# Revit family: Dachhalter BIG FOOT 400
name_source: partatom
category: HLS-Bauteile
units: mm (PartAtom-declared; Revit-internal decimal feet)

## family parameters
Arbeitsebenenbasiert = Ja
Beim Laden mit Abzugskörper schneiden = Nein
Bemaßung runder Anschluss = Durchmesser verwenden
Beschriftungsausrichtung beibehalten = Nein
Gemeinsam genutzt = Ja
Immer vertikal = Nein
Klassifizierung = Keine
Raumberechnungspunkt = Nein
Teiletyp = Normal

## types (1)
- Dachhalter BIG FOOT 400
    Artikelnummer = 08197625
    Breite Platte = 400 mm  [stored 1.31234 ft]
    EAN = 4250928468925
    Fabrikat = MEFA
    Gewicht = 1,90 kg
    Gewicht pro Bauteil = 1,90 kg
    Kurztext1 = Dachhalter BIG FOOT® 400
    Kurztext2 = für C-Profil 45/45
    Länge Platte = 400 mm  [stored 1.31234 ft]
    Material = Kunststoff
    Materialname = Polyamid 6
    Mengeneinheit = St
    Profil = C-Profil
    Profiltyp = 45
    Vorgabe-Ansicht = 1219 mm
    max. Temperaturbeständigkeit = 80 °C
    passend für = C-Profil 45/45
    vpe = 2

note: [stored X ft] marks values corroborated as IEEE doubles in the binary element streams (Revit-internal decimal feet)
